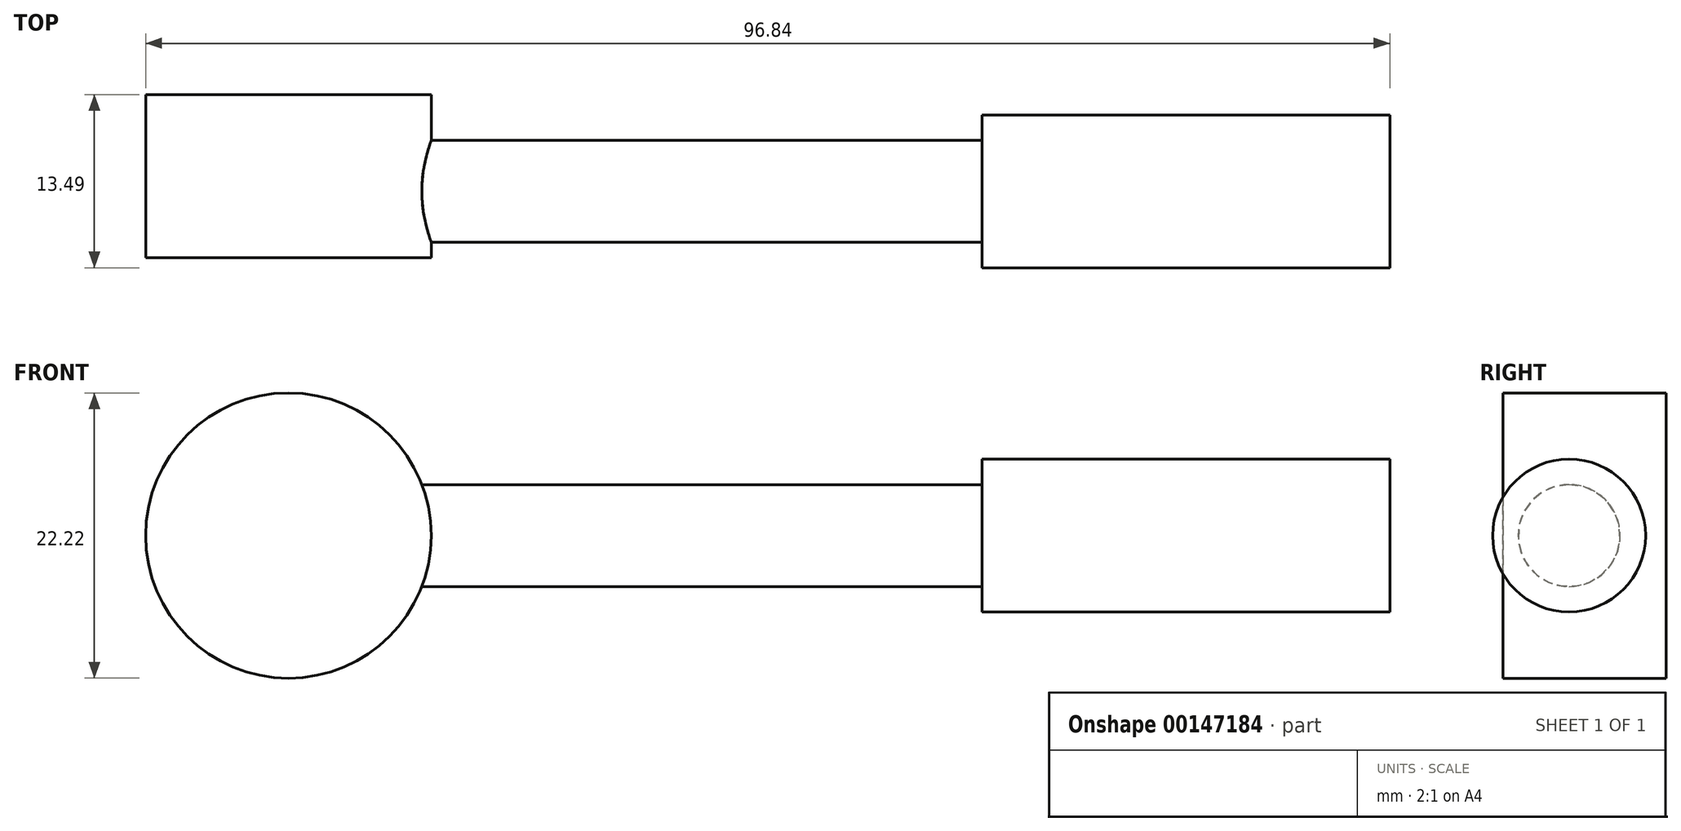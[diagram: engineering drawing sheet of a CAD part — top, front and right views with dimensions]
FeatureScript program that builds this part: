
annotation { "Feature Type Name" : "Feature", "Feature Type Description" : "" }
export const myFeature = defineFeature(function(context is Context, id is Id, definition is map)
    precondition{}
    {
        {
            var Q0;
            Q0=qCreatedBy(makeId("Front.planeOp"),FACE);
            var sketch = newSketch(context, id + "F0", { "sketchPlane" : qUnion([Q0])});
            skCircle(sketch, "E0", {"center": v(0, 0) * mm, "radius": 11.11 * mm});
            skSolve(sketch);
        }
        {
            var Q0;
            Q0=makeQuery(id+"F0.imprint","IMPRINT",FACE,{"disambiguationData":[TD([[makeQuery(id+"F0.imprint","IMPRINT",EDGE,{"derivedFrom":sQuery(id+"F0.wireOp",EDGE,"E0")}),1.0]])]});
            extrude(context, id + "F1", {"entities" : qUnion([Q0]), "depth" : 12.7 * mm});
        }
        {
            var Q0;
            Q0=qCreatedBy(makeId("Right.planeOp"),FACE);
            var sketch = newSketch(context, id + "F2", { "sketchPlane" : qUnion([Q0])});
            skCircle(sketch, "E1", {"center": v(-7.54, 0) * mm, "radius": 3.97 * mm});
            skSolve(sketch);
        }
        {
            var Q0;
            Q0=makeQuery(id+"F2.imprint","IMPRINT",FACE,{"disambiguationData":[TD([[makeQuery(id+"F2.imprint","IMPRINT",EDGE,{"derivedFrom":sQuery(id+"F2.wireOp",EDGE,"E1")}),1.0]])]});
            extrude(context, id + "F3", {"entities" : qUnion([Q0]), "operationType" : NewBodyOperationType.ADD, "depth" : 53.97 * mm});
        }
        {
            var Q0;
            Q0=makeQuery(id+"F3.opExtrude","CAP_FACE",FACE,{"disambiguationData":[OSD([sQuery(id+"F2.wireOp",EDGE,"E1")])],"isStart":false});
            var sketch = newSketch(context, id + "F4", { "sketchPlane" : qUnion([Q0])});
            skCircle(sketch, "E2", {"center": v(-7.54, 0) * mm, "radius": 5.95 * mm});
            skSolve(sketch);
        }
        {
            var Q0;
            Q0=makeQuery(id+"F4.imprint","IMPRINT",FACE,{"disambiguationData":[TD([[makeQuery(id+"F4.imprint","IMPRINT",EDGE,{"derivedFrom":sQuery(id+"F4.wireOp",EDGE,"E2")}),1.0]])]});
            var Q1;
            Q1=makeQuery(id+"F4.imprint","IMPRINT",FACE,{"disambiguationData":[TD([[makeQuery(id+"F4.imprint","IMPRINT",EDGE,{"derivedFrom":makeQuery(id+"F3.opExtrude","CAP_EDGE",EDGE,{"disambiguationData":[OSD([sQuery(id+"F2.wireOp",EDGE,"E1")])],"isStart":false})}),1.0]])]});
            extrude(context, id + "F5", {"entities" : qUnion([Q0, Q1]), "operationType" : NewBodyOperationType.ADD, "depth" : 31.75 * mm});
        }
    });
